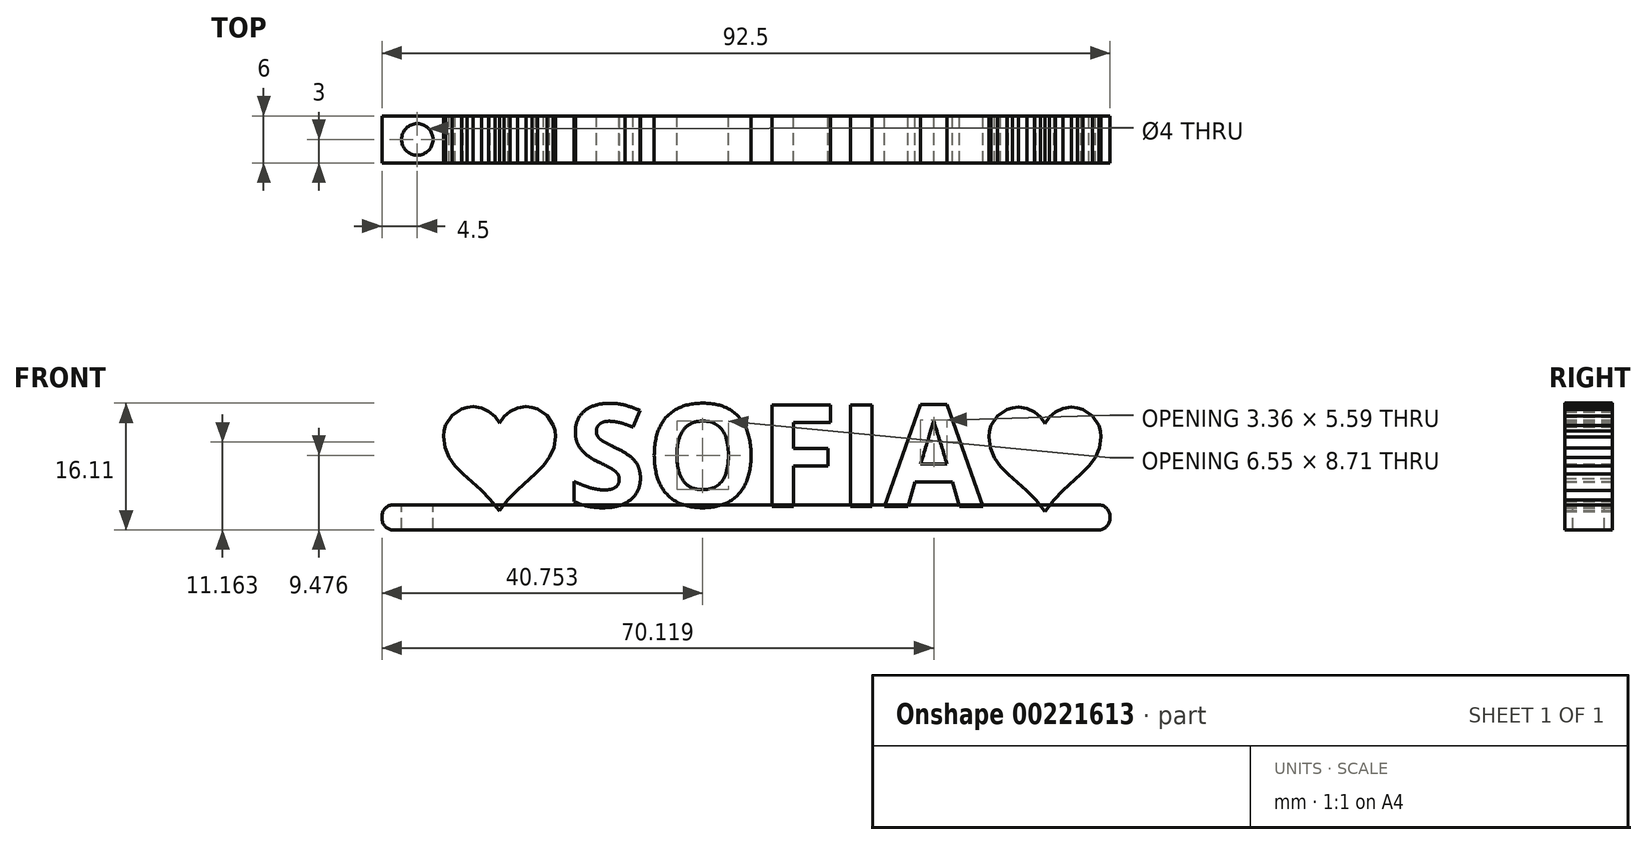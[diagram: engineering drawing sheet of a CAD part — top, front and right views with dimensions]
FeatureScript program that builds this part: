
annotation { "Feature Type Name" : "Feature", "Feature Type Description" : "" }
export const myFeature = defineFeature(function(context is Context, id is Id, definition is map)
    precondition{}
    {
        {
            var Q0;
            Q0=qCreatedBy(makeId("Front.planeOp"),FACE);
            var sketch = newSketch(context, id + "F0", { "sketchPlane" : qUnion([Q0])});
            skText(sketch, "E0", { "text": "   SOFIA", "fontName": "OpenSans-Bold.ttf"});
            skLineSegment(sketch, "E1", {"start": v(52.97, 12.6) * mm, "end": v(52.22, 12.52) * mm});
            skLineSegment(sketch, "E2", {"start": v(52.22, 12.52) * mm, "end": v(51.5, 12.3) * mm});
            skLineSegment(sketch, "E3", {"start": v(51.5, 12.3) * mm, "end": v(50.31, 11.5) * mm});
            skLineSegment(sketch, "E4", {"start": v(50.31, 11.5) * mm, "end": v(49.5, 10.3) * mm});
            skLineSegment(sketch, "E5", {"start": v(49.5, 10.3) * mm, "end": v(49.28, 9.59) * mm});
            skLineSegment(sketch, "E6", {"start": v(49.28, 9.59) * mm, "end": v(49.2, 8.83) * mm});
            skLineSegment(sketch, "E7", {"start": v(49.2, 8.83) * mm, "end": v(49.4, 7.39) * mm});
            skLineSegment(sketch, "E8", {"start": v(49.4, 7.39) * mm, "end": v(49.92, 6.16) * mm});
            skLineSegment(sketch, "E9", {"start": v(49.92, 6.16) * mm, "end": v(50.7, 5.08) * mm});
            skLineSegment(sketch, "E10", {"start": v(50.7, 5.08) * mm, "end": v(51.69, 4.08) * mm});
            skLineSegment(sketch, "E11", {"start": v(51.69, 4.08) * mm, "end": v(53.98, 2.03) * mm});
            skLineSegment(sketch, "E12", {"start": v(53.98, 2.03) * mm, "end": v(55.17, 0.82) * mm});
            skLineSegment(sketch, "E13", {"start": v(55.17, 0.82) * mm, "end": v(56.3, -0.59) * mm});
            skLineSegment(sketch, "E14", {"start": v(56.3, -0.59) * mm, "end": v(56.33, -0.65) * mm});
            skLineSegment(sketch, "E15", {"start": v(56.33, -0.65) * mm, "end": v(56.38, -0.59) * mm});
            skLineSegment(sketch, "E16", {"start": v(56.38, -0.59) * mm, "end": v(57.46, 0.82) * mm});
            skLineSegment(sketch, "E17", {"start": v(57.46, 0.82) * mm, "end": v(58.62, 2.03) * mm});
            skLineSegment(sketch, "E18", {"start": v(58.62, 2.03) * mm, "end": v(60.92, 4.12) * mm});
            skLineSegment(sketch, "E19", {"start": v(60.92, 4.12) * mm, "end": v(61.92, 5.13) * mm});
            skLineSegment(sketch, "E20", {"start": v(61.92, 5.13) * mm, "end": v(62.73, 6.21) * mm});
            skLineSegment(sketch, "E21", {"start": v(62.73, 6.21) * mm, "end": v(63.26, 7.42) * mm});
            skLineSegment(sketch, "E22", {"start": v(63.26, 7.42) * mm, "end": v(63.46, 8.83) * mm});
            skLineSegment(sketch, "E23", {"start": v(63.46, 8.83) * mm, "end": v(63.38, 9.59) * mm});
            skLineSegment(sketch, "E24", {"start": v(63.38, 9.59) * mm, "end": v(63.16, 10.3) * mm});
            skLineSegment(sketch, "E25", {"start": v(63.16, 10.3) * mm, "end": v(62.36, 11.5) * mm});
            skLineSegment(sketch, "E26", {"start": v(62.36, 11.5) * mm, "end": v(61.16, 12.3) * mm});
            skLineSegment(sketch, "E27", {"start": v(61.16, 12.3) * mm, "end": v(60.45, 12.52) * mm});
            skLineSegment(sketch, "E28", {"start": v(60.45, 12.52) * mm, "end": v(59.7, 12.6) * mm});
            skLineSegment(sketch, "E29", {"start": v(59.7, 12.6) * mm, "end": v(58.63, 12.44) * mm});
            skLineSegment(sketch, "E30", {"start": v(58.63, 12.44) * mm, "end": v(57.7, 12.01) * mm});
            skLineSegment(sketch, "E31", {"start": v(57.7, 12.01) * mm, "end": v(56.91, 11.35) * mm});
            skLineSegment(sketch, "E32", {"start": v(56.91, 11.35) * mm, "end": v(56.33, 10.5) * mm});
            skLineSegment(sketch, "E33", {"start": v(56.33, 10.5) * mm, "end": v(55.76, 11.35) * mm});
            skLineSegment(sketch, "E34", {"start": v(55.76, 11.35) * mm, "end": v(54.98, 12.01) * mm});
            skLineSegment(sketch, "E35", {"start": v(54.98, 12.01) * mm, "end": v(54.04, 12.44) * mm});
            skLineSegment(sketch, "E36", {"start": v(54.04, 12.44) * mm, "end": v(52.97, 12.6) * mm});
            skLineSegment(sketch, "E37", {"start": v(49.6, 13.02) * mm, "end": v(74.89, 13.02) * mm, "construction": true});
            skLineSegment(sketch, "E38", {"start": v(-16.32, 12.66) * mm, "end": v(-17.08, 12.59) * mm});
            skLineSegment(sketch, "E39", {"start": v(-17.08, 12.59) * mm, "end": v(-17.78, 12.37) * mm});
            skLineSegment(sketch, "E40", {"start": v(-17.78, 12.37) * mm, "end": v(-18.98, 11.56) * mm});
            skLineSegment(sketch, "E41", {"start": v(-18.98, 11.56) * mm, "end": v(-19.79, 10.36) * mm});
            skLineSegment(sketch, "E42", {"start": v(-19.79, 10.36) * mm, "end": v(-20, 9.65) * mm});
            skLineSegment(sketch, "E43", {"start": v(-20, 9.65) * mm, "end": v(-20.09, 8.9) * mm});
            skLineSegment(sketch, "E44", {"start": v(-20.09, 8.9) * mm, "end": v(-19.9, 7.45) * mm});
            skLineSegment(sketch, "E45", {"start": v(-19.9, 7.45) * mm, "end": v(-19.38, 6.22) * mm});
            skLineSegment(sketch, "E46", {"start": v(-19.38, 6.22) * mm, "end": v(-18.6, 5.15) * mm});
            skLineSegment(sketch, "E47", {"start": v(-18.6, 5.15) * mm, "end": v(-17.6, 4.15) * mm});
            skLineSegment(sketch, "E48", {"start": v(-17.6, 4.15) * mm, "end": v(-15.31, 2.09) * mm});
            skLineSegment(sketch, "E49", {"start": v(-15.31, 2.09) * mm, "end": v(-14.13, 0.89) * mm});
            skLineSegment(sketch, "E50", {"start": v(-14.13, 0.89) * mm, "end": v(-13, -0.52) * mm});
            skLineSegment(sketch, "E51", {"start": v(-13, -0.52) * mm, "end": v(-12.96, -0.59) * mm});
            skLineSegment(sketch, "E52", {"start": v(-12.96, -0.59) * mm, "end": v(-12.92, -0.52) * mm});
            skLineSegment(sketch, "E53", {"start": v(-12.92, -0.52) * mm, "end": v(-11.84, 0.89) * mm});
            skLineSegment(sketch, "E54", {"start": v(-11.84, 0.89) * mm, "end": v(-10.67, 2.1) * mm});
            skLineSegment(sketch, "E55", {"start": v(-10.67, 2.1) * mm, "end": v(-8.37, 4.19) * mm});
            skLineSegment(sketch, "E56", {"start": v(-8.37, 4.19) * mm, "end": v(-7.37, 5.2) * mm});
            skLineSegment(sketch, "E57", {"start": v(-7.37, 5.2) * mm, "end": v(-6.56, 6.28) * mm});
            skLineSegment(sketch, "E58", {"start": v(-6.56, 6.28) * mm, "end": v(-6.03, 7.49) * mm});
            skLineSegment(sketch, "E59", {"start": v(-6.03, 7.49) * mm, "end": v(-5.83, 8.9) * mm});
            skLineSegment(sketch, "E60", {"start": v(-5.83, 8.9) * mm, "end": v(-5.91, 9.65) * mm});
            skLineSegment(sketch, "E61", {"start": v(-5.91, 9.65) * mm, "end": v(-6.13, 10.36) * mm});
            skLineSegment(sketch, "E62", {"start": v(-6.13, 10.36) * mm, "end": v(-6.94, 11.56) * mm});
            skLineSegment(sketch, "E63", {"start": v(-6.94, 11.56) * mm, "end": v(-8.13, 12.37) * mm});
            skLineSegment(sketch, "E64", {"start": v(-8.13, 12.37) * mm, "end": v(-8.84, 12.59) * mm});
            skLineSegment(sketch, "E65", {"start": v(-8.84, 12.59) * mm, "end": v(-9.6, 12.66) * mm});
            skLineSegment(sketch, "E66", {"start": v(-9.6, 12.66) * mm, "end": v(-10.66, 12.5) * mm});
            skLineSegment(sketch, "E67", {"start": v(-10.66, 12.5) * mm, "end": v(-11.6, 12.08) * mm});
            skLineSegment(sketch, "E68", {"start": v(-11.6, 12.08) * mm, "end": v(-12.38, 11.41) * mm});
            skLineSegment(sketch, "E69", {"start": v(-12.38, 11.41) * mm, "end": v(-12.96, 10.56) * mm});
            skLineSegment(sketch, "E70", {"start": v(-12.96, 10.56) * mm, "end": v(-13.54, 11.41) * mm});
            skLineSegment(sketch, "E71", {"start": v(-13.54, 11.41) * mm, "end": v(-14.32, 12.08) * mm});
            skLineSegment(sketch, "E72", {"start": v(-14.32, 12.08) * mm, "end": v(-15.26, 12.5) * mm});
            skLineSegment(sketch, "E73", {"start": v(-15.26, 12.5) * mm, "end": v(-16.32, 12.66) * mm});
            const initialGuessF0  = {"E0": [-0.0184, 0, 1, 0, 0.01302]};
            skSetInitialGuess(sketch, initialGuessF0);
            skSolve(sketch);
        }
        {
            var Q0;
            Q0=qSketchRegion(id+"F0",true);
            extrude(context, id + "F1", {"entities" : qUnion([Q0]), "endBound" : BoundingType.SYMMETRIC, "depth" : 6 * mm});
        }
        {
            var Q0;
            Q0=qCreatedBy(makeId("Top.planeOp"),FACE);
            var sketch = newSketch(context, id + "F2", { "sketchPlane" : qUnion([Q0])});
            skLineSegment(sketch, "E74.bottom", {"start": v(-20.4, 3) * mm, "end": v(64.6, 3) * mm});
            skLineSegment(sketch, "E74.top", {"start": v(-20.4, -3) * mm, "end": v(64.6, -3) * mm});
            skLineSegment(sketch, "E74.left", {"start": v(-20.4, 3) * mm, "end": v(-20.4, -3) * mm});
            skLineSegment(sketch, "E74.right", {"start": v(64.6, 3) * mm, "end": v(64.6, -3) * mm});
            skSolve(sketch);
        }
        {
            var Q0;
            Q0=makeQuery(id+"F2.imprint","IMPRINT",FACE,{"disambiguationData":[TD([[makeQuery(id+"F2.imprint","IMPRINT",EDGE,{"derivedFrom":sQuery(id+"F2.wireOp",EDGE,"E74.bottom")}),-1.0]])]});
            extrude(context, id + "F3", {"entities" : qUnion([Q0]), "depth" : 0.2 * mm});
        }
        {
            var Q0;
            Q0=makeQuery(id+"F3.opExtrude","CAP_FACE",FACE,{"disambiguationData":[OSD([sQuery(id+"F2.wireOp",EDGE,"E74.bottom"),sQuery(id+"F2.wireOp",EDGE,"E74.top"),sQuery(id+"F2.wireOp",EDGE,"E74.left"),sQuery(id+"F2.wireOp",EDGE,"E74.right")])],"isStart":true});
            extrude(context, id + "F4", {"entities" : qUnion([Q0]), "depth" : 3 * mm});
        }
        {
            var Q0;
            {var subQ0=sQuery(id+"F2.wireOp",EDGE,"E74.left");Q0=makeQuery(id+"FaVoHrOpcFZXiYX_6.opBoolean","MERGE",FACE,{"derivedFrom":[makeQuery(id+"F3.opExtrude","SWEPT_FACE",FACE,{"disambiguationData":[OSD([subQ0])]}),makeQuery(id+"F4.opExtrude","SWEPT_FACE",FACE,{"disambiguationData":[OSD([subQ0])]})]});}
            var sketch = newSketch(context, id + "F5", { "sketchPlane" : qUnion([Q0])});
            skLineSegment(sketch, "E75.bottom", {"start": v(-3, -3) * mm, "end": v(3, -3) * mm});
            skLineSegment(sketch, "E75.top", {"start": v(-3, 0.2) * mm, "end": v(3, 0.2) * mm});
            skLineSegment(sketch, "E75.left", {"start": v(-3, -3) * mm, "end": v(-3, 0.2) * mm});
            skLineSegment(sketch, "E75.right", {"start": v(3, -3) * mm, "end": v(3, 0.2) * mm});
            skSolve(sketch);
        }
        {
            var Q0;
            Q0=qSketchRegion(id+"F5",true);
            extrude(context, id + "F6", {"entities" : qUnion([Q0]), "operationType" : NewBodyOperationType.ADD, "depth" : 7.5 * mm});
        }
        {
            var Q0;
            Q0=makeQuery(id+"F6.opExtrude","CAP_EDGE",EDGE,{"disambiguationData":[OSD([sQuery(id+"F5.wireOp",EDGE,"E75.bottom")])],"isStart":false});
            var Q1;
            Q1=makeQuery(id+"F6.opExtrude","CAP_EDGE",EDGE,{"disambiguationData":[OSD([sQuery(id+"F5.wireOp",EDGE,"E75.top")])],"isStart":false});
            var Q2;
            Q2=makeQuery(id+"F4.opExtrude","CAP_EDGE",EDGE,{"disambiguationData":[OSD([sQuery(id+"F2.wireOp",EDGE,"E74.right")])],"isStart":false});
            fillet(context, id + "F7", {"entities" : qUnion([Q0, Q1, Q2]), "radius" : 1.5 * mm, "tangentPropagation" : true, "allowEdgeOverflow" : false});
        }
        {
            var Q0;
            {var subQ19=sQuery(id+"F2.wireOp",EDGE,"E74.top");var subQ20=sQuery(id+"F2.wireOp",EDGE,"E74.bottom");var subQ63=sQuery(id+"F0.wireOp",EDGE,"E0.sketch_text.stroke-2");var subQ66=sQuery(id+"F2.wireOp",EDGE,"E74.left");Q0=makeQuery(id+"F6.boolean.opBoolean","MERGE",FACE,{"derivedFrom":[makeQuery(id+"FaVoHrOpcFZXiYX_6.opBoolean","SPLIT",FACE,{"disambiguationData":[TD([makeQuery(id+"F1.opExtrude","SWEPT_FACE",FACE,{"disambiguationData":[OSD([subQ63])]})])],"derivedFrom":makeQuery(id+"F3.opExtrude","CAP_FACE",FACE,{"disambiguationData":[OSD([subQ20,subQ19,subQ66,sQuery(id+"F2.wireOp",EDGE,"E74.right")])],"isStart":false})}),makeQuery(id+"F6.opExtrude","SWEPT_FACE",FACE,{"disambiguationData":[OSD([sQuery(id+"F5.wireOp",EDGE,"E75.top")])]})]});}
            var sketch = newSketch(context, id + "F8", { "sketchPlane" : qUnion([Q0])});
            skCircle(sketch, "E76", {"center": v(-23.4, 0) * mm, "radius": 2 * mm});
            skSolve(sketch);
        }
        {
            var Q0;
            Q0=makeQuery(id+"F8.imprint","IMPRINT",FACE,{"disambiguationData":[TD([[makeQuery(id+"F8.imprint","IMPRINT",EDGE,{"derivedFrom":sQuery(id+"F8.wireOp",EDGE,"E76")}),1.0]])]});
            extrude(context, id + "F9", {"entities" : qUnion([Q0]), "operationType" : NewBodyOperationType.REMOVE, "oppositeDirection" : true, "depth" : 4 * mm});
        }
        {
            var Q0;
            Q0=makeQuery(id+"F3.opExtrude","CAP_EDGE",EDGE,{"disambiguationData":[OSD([sQuery(id+"F2.wireOp",EDGE,"E74.right")])],"isStart":false});
            fillet(context, id + "F10", {"entities" : qUnion([Q0]), "radius" : 1.5 * mm, "tangentPropagation" : true, "allowEdgeOverflow" : false});
        }
    });
